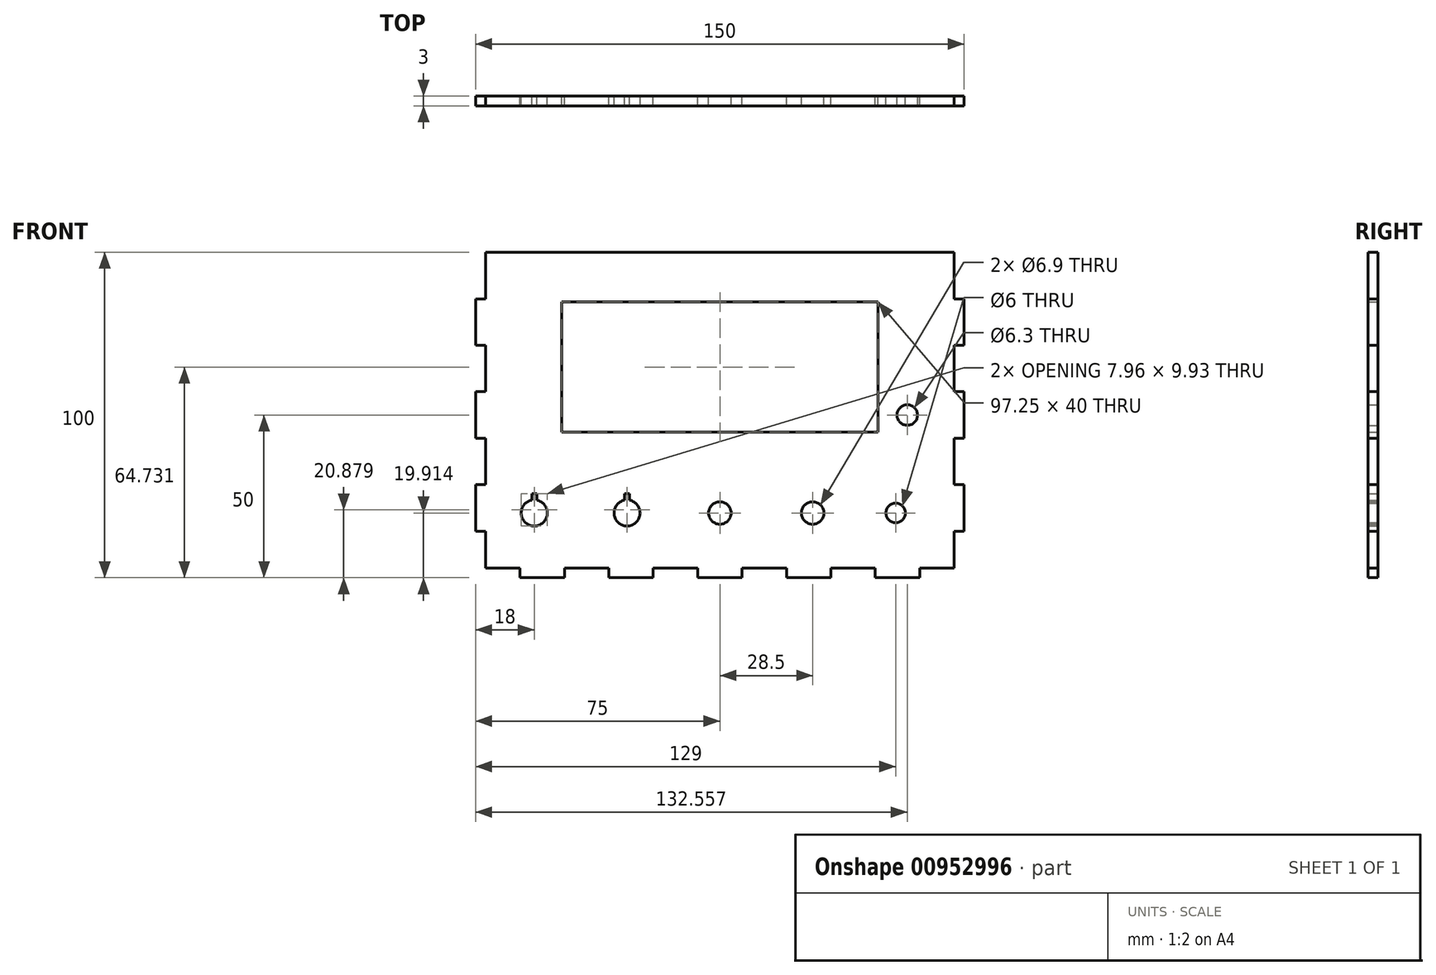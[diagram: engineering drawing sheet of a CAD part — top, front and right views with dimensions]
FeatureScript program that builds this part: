
annotation { "Feature Type Name" : "Feature", "Feature Type Description" : "" }
export const myFeature = defineFeature(function(context is Context, id is Id, definition is map)
    precondition{}
    {
        {
            var Q0;
            Q0=qCreatedBy(makeId("Front.planeOp"),FACE);
            var sketch = newSketch(context, id + "F0", { "sketchPlane" : qUnion([Q0])});
            skLineSegment(sketch, "E0.bottom", {"start": v(61.36, -50) * mm, "end": v(47.73, -50) * mm});
            skLineSegment(sketch, "E0.top", {"start": v(72, 50) * mm, "end": v(-72, 50) * mm});
            skLineSegment(sketch, "E0.right", {"start": v(-75, -35.71) * mm, "end": v(-75, -21.43) * mm});
            skPoint(sketch, "E0.middle", {"position": v(0, 0) * mm});
            skLineSegment(sketch, "E1", {"start": v(-72, -47) * mm, "end": v(-61.36, -47) * mm});
            skLineSegment(sketch, "E2", {"start": v(-61.36, -47) * mm, "end": v(-61.36, -50) * mm});
            skLineSegment(sketch, "E3", {"start": v(-47.73, -47) * mm, "end": v(-47.73, -50) * mm});
            skLineSegment(sketch, "E4", {"start": v(-34.1, -47) * mm, "end": v(-34.1, -50) * mm});
            skLineSegment(sketch, "E5", {"start": v(-20.45, -47) * mm, "end": v(-20.45, -50) * mm});
            skLineSegment(sketch, "E6", {"start": v(-6.82, -47) * mm, "end": v(-6.82, -50) * mm});
            skLineSegment(sketch, "E7", {"start": v(6.82, -47) * mm, "end": v(6.82, -50) * mm});
            skLineSegment(sketch, "E8", {"start": v(34.1, -47) * mm, "end": v(34.1, -50) * mm});
            skLineSegment(sketch, "E9", {"start": v(47.73, -47) * mm, "end": v(47.73, -50) * mm});
            skLineSegment(sketch, "E10", {"start": v(20.45, -47) * mm, "end": v(20.45, -50) * mm});
            skLineSegment(sketch, "E11", {"start": v(61.36, -47) * mm, "end": v(61.36, -50) * mm});
            skLineSegment(sketch, "E12.trimOffspring", {"start": v(-47.73, -47) * mm, "end": v(-34.1, -47) * mm});
            skLineSegment(sketch, "E13.trimOffspring", {"start": v(-47.73, -50) * mm, "end": v(-61.36, -50) * mm});
            skLineSegment(sketch, "E14.trimOffspring", {"start": v(-20.45, -47) * mm, "end": v(-6.82, -47) * mm});
            skLineSegment(sketch, "E15.trimOffspring", {"start": v(-20.45, -50) * mm, "end": v(-34.1, -50) * mm});
            skLineSegment(sketch, "E16.trimOffspring", {"start": v(6.82, -47) * mm, "end": v(20.45, -47) * mm});
            skLineSegment(sketch, "E17.trimOffspring", {"start": v(6.82, -50) * mm, "end": v(-6.82, -50) * mm});
            skLineSegment(sketch, "E18.trimOffspring", {"start": v(34.1, -47) * mm, "end": v(47.73, -47) * mm});
            skLineSegment(sketch, "E19.trimOffspring", {"start": v(34.1, -50) * mm, "end": v(20.45, -50) * mm});
            skLineSegment(sketch, "E20.trimOffspring", {"start": v(61.36, -47) * mm, "end": v(72, -47) * mm});
            skPoint(sketch, "E21.orphan", {"position": v(75, -50) * mm});
            skPoint(sketch, "E22.orphan", {"position": v(-75, -50) * mm});
            skLineSegment(sketch, "E23", {"start": v(-72, 50) * mm, "end": v(-72, 35.71) * mm});
            skLineSegment(sketch, "E24", {"start": v(-75, 35.71) * mm, "end": v(-72, 35.71) * mm});
            skLineSegment(sketch, "E25", {"start": v(-75, 21.43) * mm, "end": v(-72, 21.43) * mm});
            skLineSegment(sketch, "E26", {"start": v(-75, 7.14) * mm, "end": v(-72, 7.14) * mm});
            skLineSegment(sketch, "E27", {"start": v(-75, -7.14) * mm, "end": v(-72, -7.14) * mm});
            skLineSegment(sketch, "E28", {"start": v(-75, -21.43) * mm, "end": v(-72, -21.43) * mm});
            skLineSegment(sketch, "E29", {"start": v(-75, -35.71) * mm, "end": v(-72, -35.71) * mm});
            skLineSegment(sketch, "E30.trimOffspring", {"start": v(-72, -35.71) * mm, "end": v(-72, -47) * mm});
            skLineSegment(sketch, "E31.trimOffspring", {"start": v(-75, -7.14) * mm, "end": v(-75, 7.14) * mm});
            skLineSegment(sketch, "E32.trimOffspring", {"start": v(-72, -7.14) * mm, "end": v(-72, -21.43) * mm});
            skLineSegment(sketch, "E33.trimOffspring", {"start": v(-75, 21.43) * mm, "end": v(-75, 35.71) * mm});
            skLineSegment(sketch, "E34.trimOffspring", {"start": v(-72, 21.43) * mm, "end": v(-72, 7.14) * mm});
            skPoint(sketch, "E35.orphan", {"position": v(-75, 50) * mm});
            skLineSegment(sketch, "E36.MirrorCS", {"start": v(75, 21.43) * mm, "end": v(72, 21.43) * mm});
            skLineSegment(sketch, "E37.MirrorCS", {"start": v(75, -7.14) * mm, "end": v(72, -7.14) * mm});
            skLineSegment(sketch, "E38.MirrorCS", {"start": v(75, -35.71) * mm, "end": v(72, -35.71) * mm});
            skLineSegment(sketch, "E39.MirrorCS", {"start": v(75, 7.14) * mm, "end": v(72, 7.14) * mm});
            skLineSegment(sketch, "E40.MirrorCS", {"start": v(75, 35.71) * mm, "end": v(72, 35.71) * mm});
            skLineSegment(sketch, "E41.MirrorCS", {"start": v(75, -21.43) * mm, "end": v(72, -21.43) * mm});
            skLineSegment(sketch, "E42.MirrorCS", {"start": v(75, -7.14) * mm, "end": v(75, 7.14) * mm});
            skLineSegment(sketch, "E43.MirrorCS", {"start": v(75, 21.43) * mm, "end": v(75, 35.71) * mm});
            skLineSegment(sketch, "E44.MirrorCS", {"start": v(72, -35.71) * mm, "end": v(72, -47) * mm});
            skLineSegment(sketch, "E45.MirrorCS", {"start": v(72, -7.14) * mm, "end": v(72, -21.43) * mm});
            skLineSegment(sketch, "E46.MirrorCS", {"start": v(72, 21.43) * mm, "end": v(72, 7.14) * mm});
            skPoint(sketch, "E47.MirrorP", {"position": v(75, 50) * mm});
            skLineSegment(sketch, "E48.MirrorCS", {"start": v(72, 50) * mm, "end": v(72, 35.71) * mm});
            skLineSegment(sketch, "E49.MirrorCS", {"start": v(75, -35.71) * mm, "end": v(75, -21.43) * mm});
            skPoint(sketch, "E50.orphan", {"position": v(75, -47) * mm});
            skLineSegment(sketch, "E51.bottom", {"start": v(48.62, -5.27) * mm, "end": v(-48.62, -5.27) * mm});
            skLineSegment(sketch, "E51.top", {"start": v(48.62, 34.73) * mm, "end": v(-48.62, 34.73) * mm});
            skLineSegment(sketch, "E51.left", {"start": v(48.62, -5.27) * mm, "end": v(48.62, 34.73) * mm});
            skLineSegment(sketch, "E51.right", {"start": v(-48.62, -5.27) * mm, "end": v(-48.62, 34.73) * mm});
            skPoint(sketch, "E51.middle", {"position": v(0, 14.73) * mm});
            skCircle(sketch, "E52", {"center": v(54, -30.09) * mm, "radius": 3 * mm});
            skLineSegment(sketch, "E53", {"start": v(54, -30.09) * mm, "end": v(-66.18, -30.09) * mm, "construction": true});
            skCircle(sketch, "E54", {"center": v(0, -30.09) * mm, "radius": 3.45 * mm});
            skCircle(sketch, "E55", {"center": v(28.5, -30.09) * mm, "radius": 3.45 * mm});
            skArc(sketch, "E56", {"start": v(-57.75, -26.16) * mm, "mid": v(-57, -34.09) * mm, "end": v(-56.25, -26.16) * mm});
            skArc(sketch, "E57", {"start": v(-29.25, -26.16) * mm, "mid": v(-28.5, -34.09) * mm, "end": v(-27.75, -26.16) * mm});
            skCircle(sketch, "E58", {"center": v(57.56, 0) * mm, "radius": 3.15 * mm});
            skLineSegment(sketch, "E59", {"start": v(-57.75, -26.16) * mm, "end": v(-57.75, -24.16) * mm});
            skLineSegment(sketch, "E60", {"start": v(-57.75, -24.16) * mm, "end": v(-56.25, -24.16) * mm});
            skLineSegment(sketch, "E61", {"start": v(-56.25, -24.16) * mm, "end": v(-56.25, -26.16) * mm});
            skLineSegment(sketch, "E62", {"start": v(-29.25, -26.16) * mm, "end": v(-29.25, -24.16) * mm});
            skLineSegment(sketch, "E63", {"start": v(-29.25, -24.16) * mm, "end": v(-27.75, -24.16) * mm});
            skLineSegment(sketch, "E64", {"start": v(-27.75, -24.16) * mm, "end": v(-27.75, -26.16) * mm});
            skSolve(sketch);
        }
        {
            var Q0;
            Q0=makeQuery(id+"F0.imprint","IMPRINT",FACE,{"disambiguationData":[TD([[makeQuery(id+"F0.imprint","IMPRINT",EDGE,{"derivedFrom":sQuery(id+"F0.wireOp",EDGE,"E0.bottom")}),-1.0]])]});
            extrude(context, id + "F1", {"entities" : qUnion([Q0]), "depth" : 3 * mm, "offsetDistance" : 25 * mm});
        }
    });
